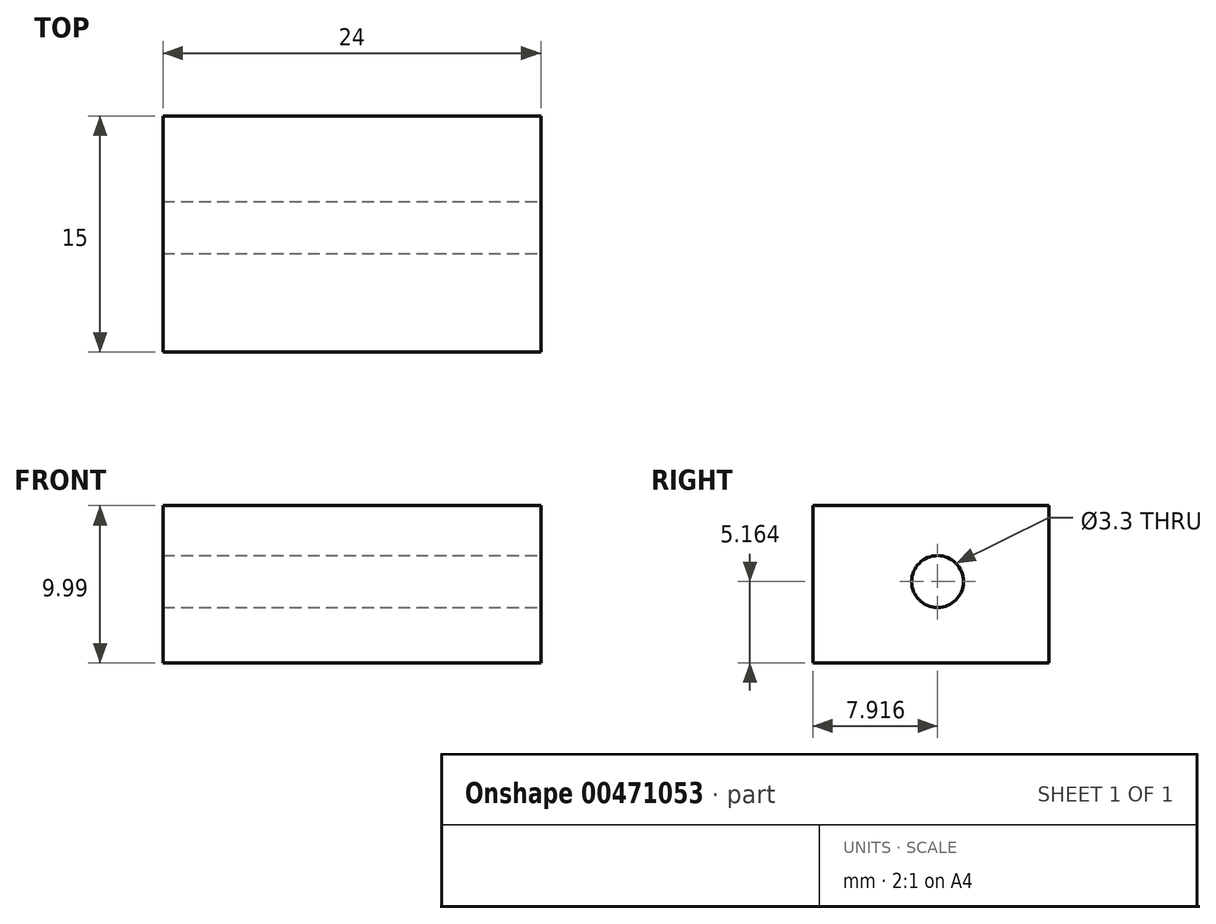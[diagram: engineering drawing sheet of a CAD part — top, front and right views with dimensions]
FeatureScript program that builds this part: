
annotation { "Feature Type Name" : "Feature", "Feature Type Description" : "" }
export const myFeature = defineFeature(function(context is Context, id is Id, definition is map)
    precondition{}
    {
        {
            var Q0;
            Q0=qCreatedBy(makeId("Top.planeOp"),FACE);
            var sketch = newSketch(context, id + "F0", { "sketchPlane" : qUnion([Q0])});
            skLineSegment(sketch, "E0.bottom", {"start": v(-24, 31.1) * mm, "end": v(0, 31.1) * mm});
            skLineSegment(sketch, "E0.top", {"start": v(-24, 16.1) * mm, "end": v(0, 16.1) * mm});
            skLineSegment(sketch, "E0.left", {"start": v(-24, 31.1) * mm, "end": v(-24, 16.1) * mm});
            skLineSegment(sketch, "E0.right", {"start": v(0, 31.1) * mm, "end": v(0, 16.1) * mm});
            skSolve(sketch);
        }
        {
            var Q0;
            Q0 = qSketchRegion(id + "F0", true);
            extrude(context, id + "F1", {"entities" : qUnion([Q0]), "depth" : 10 * mm, "offsetDistance" : 25 * mm});
        }
        {
            var Q0;
            Q0=qCreatedBy(makeId("Right.planeOp"),FACE);
            var sketch = newSketch(context, id + "F2", { "sketchPlane" : qUnion([Q0])});
            skCircle(sketch, "E1", {"center": v(24.02, 5.16) * mm, "radius": 1.65 * mm});
            skSolve(sketch);
        }
        {
            var Q0;
            Q0=sQuery(id+"F2.wireOp",VERTEX,"E1.center");
            var Q1;
            Q1=makeQuery(id+"F1.opExtrude","SWEPT_BODY",BODY,{"disambiguationData":[OSD([sQuery(id+"F0.wireOp",EDGE,"E0.bottom"),sQuery(id+"F0.wireOp",EDGE,"E0.top"),sQuery(id+"F0.wireOp",EDGE,"E0.left"),sQuery(id+"F0.wireOp",EDGE,"E0.right")])]});
            hole(context, id + "F3", {"style" : HoleStyle.SIMPLE, "endStyle" : HoleEndStyle.THROUGH, "holeDiameter" : 3.3 * mm, "isTappedThrough" : true, "tappedDepth" : 12 * mm, "tapClearance" : 3, "locations" : qUnion([Q0]), "scope" : qUnion([Q1])});
        }
    });
